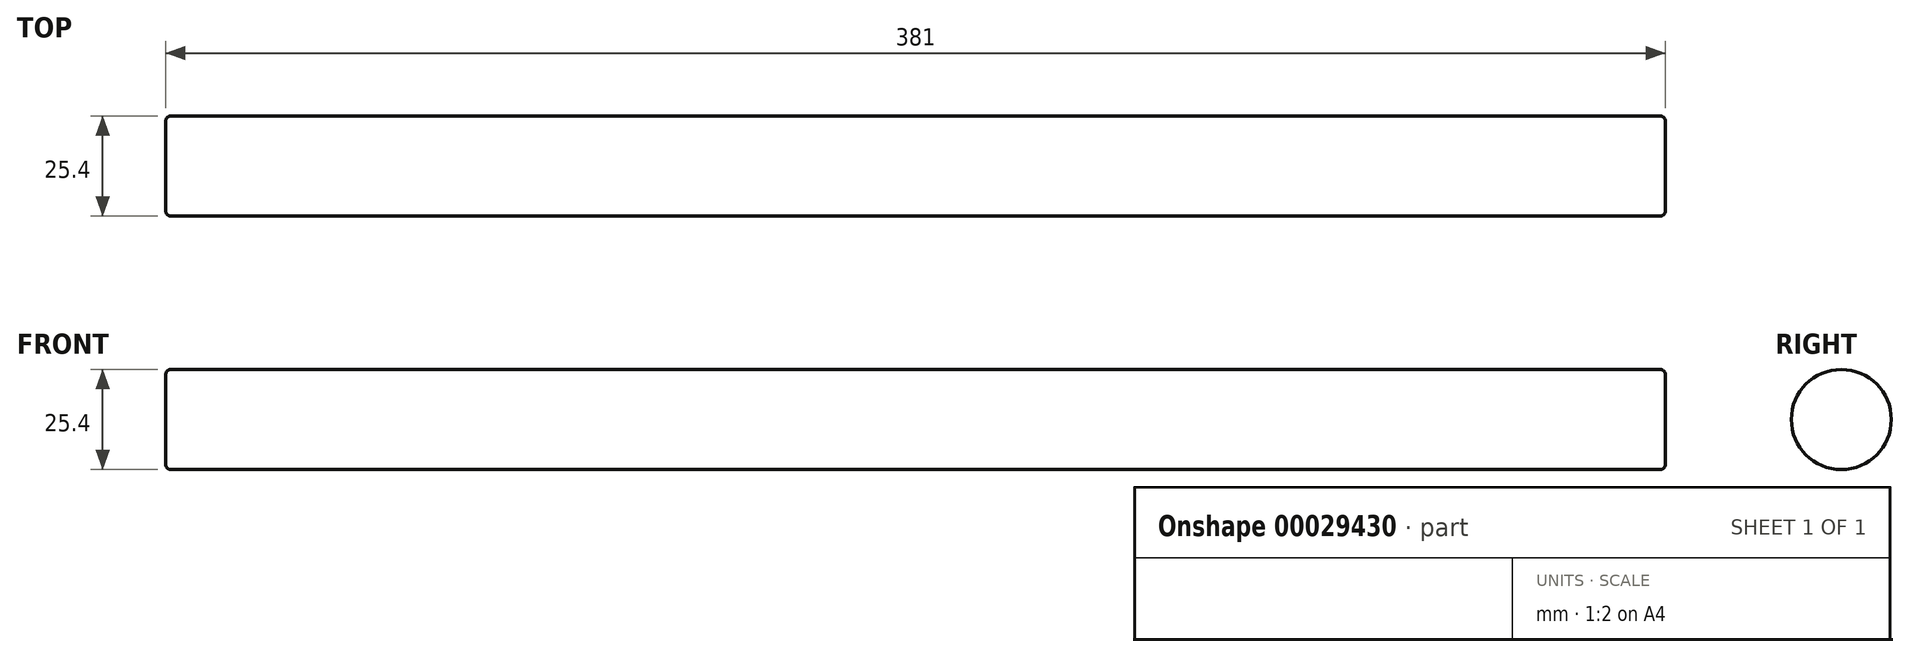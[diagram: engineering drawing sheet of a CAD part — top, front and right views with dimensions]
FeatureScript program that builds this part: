
annotation { "Feature Type Name" : "Feature", "Feature Type Description" : "" }
export const myFeature = defineFeature(function(context is Context, id is Id, definition is map)
    precondition{}
    {
        {
            var Q0;
            Q0=qCreatedBy(makeId("Right.planeOp"),FACE);
            var sketch = newSketch(context, id + "F0", { "sketchPlane" : qUnion([Q0])});
            skCircle(sketch, "E0", {"center": v(0, 0) * mm, "radius": 12.7 * mm});
            skSolve(sketch);
        }
        {
            var Q0;
            Q0 = qSketchRegion(id + "F0", true);
            extrude(context, id + "F1", {"entities" : qUnion([Q0]), "depth" : 381 * mm});
        }
        {
            var Q0;
            Q0=makeQuery(id+"F1.opExtrude","CAP_EDGE",EDGE,{"disambiguationData":[OSD([sQuery(id+"F0.wireOp",EDGE,"E0")])],"isStart":true});
            var Q1;
            Q1=makeQuery(id+"F1.opExtrude","CAP_EDGE",EDGE,{"disambiguationData":[OSD([sQuery(id+"F0.wireOp",EDGE,"E0")])],"isStart":false});
            fillet(context, id + "F2", {"entities" : qUnion([Q0, Q1]), "radius" : 1.27 * mm, "tangentPropagation" : true, "allowEdgeOverflow" : false});
        }
    });
